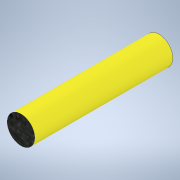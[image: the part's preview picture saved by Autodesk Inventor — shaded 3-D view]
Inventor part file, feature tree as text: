
AUTODESK INVENTOR PART (.ipt)
format: ipt  version: 2020 (Build 240168000, 168)  size: 95,744 bytes
history: native  units: in
note: dims shown in document units (in); Inventor stores cm internally (conversion verified against a paired STEP export)
features: extrude x1, sketch x1
ambient origin geometry x8: Origin, YZ Plane, XZ Plane, XY Plane, X Axis, Y Axis, Z Axis, Center Point
bodies: Solid1 (feature_tree)
feature tree (2):
  extrude  "Extrusion1"  Depth=1.9685in TaperAngle=0.0deg
  sketch  "Sketch1"  dims[d0=0.3937in d1=1.9685in d2=0.0in]
